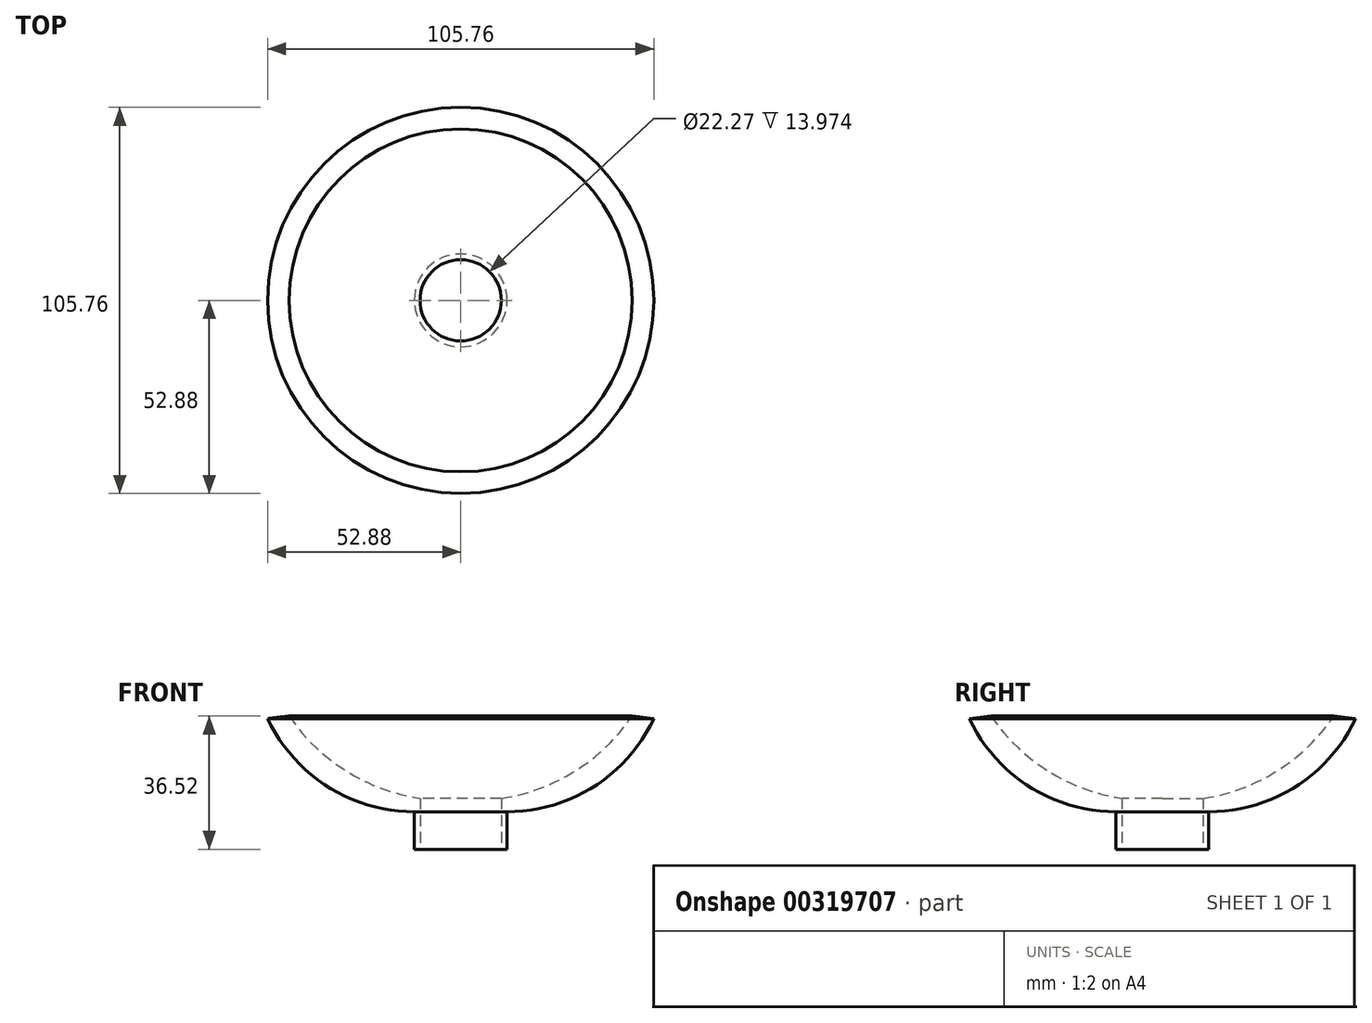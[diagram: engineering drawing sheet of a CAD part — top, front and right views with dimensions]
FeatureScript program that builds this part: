
annotation { "Feature Type Name" : "Feature", "Feature Type Description" : "" }
export const myFeature = defineFeature(function(context is Context, id is Id, definition is map)
    precondition{}
    {
        {
            var Q0;
            Q0=qCreatedBy(makeId("Front.planeOp"),FACE);
            var sketch = newSketch(context, id + "F0", { "sketchPlane" : qUnion([Q0])});
            skLineSegment(sketch, "E0", {"start": v(0, 0) * mm, "end": v(-12.7, 0) * mm});
            skLineSegment(sketch, "E1", {"start": v(-12.7, 0) * mm, "end": v(-12.7, 10.28) * mm});
            skLineSegment(sketch, "E2", {"start": v(0, 0) * mm, "end": v(0, 10.28) * mm});
            skArc(sketch, "E3", {"start": v(0, 10.28) * mm, "mid": v(23.79, 17.23) * mm, "end": v(40.18, 35.8) * mm});
            skLineSegment(sketch, "E4", {"start": v(-12.7, 10.28) * mm, "end": v(-12.7, 13.47) * mm});
            skArc(sketch, "E5", {"start": v(-12.7, 13.47) * mm, "mid": v(13.83, 18.8) * mm, "end": v(34.27, 36.52) * mm});
            skPoint(sketch, "E6.orphan", {"position": v(-12.7, 16.66) * mm});
            skLineSegment(sketch, "E7", {"start": v(34.27, 36.52) * mm, "end": v(40.18, 35.8) * mm});
            skSolve(sketch);
        }
        {
            var Q0;
            Q0 = qSketchRegion(id + "F0", true);
            var Q1;
            Q1=sQuery(id+"F0.wireOp",EDGE,"E1");
            revolve(context, id + "F1", {"entities" : qUnion([Q0]), "axis" : qUnion([Q1]), "revolveType" : RevolveType.FULL});
        }
        {
            var Q0;
            Q0=makeQuery(id+"F1.opRevolve","SWEPT_FACE",FACE,{"disambiguationData":[OSD([sQuery(id+"F0.wireOp",EDGE,"E0")])]});
            var sketch = newSketch(context, id + "F2", { "sketchPlane" : qUnion([Q0])});
            skCircle(sketch, "E8", {"center": v(-12.7, 0) * mm, "radius": 11.13 * mm});
            skSolve(sketch);
        }
        {
            var Q0;
            Q0 = qSketchRegion(id + "F2", true);
            extrude(context, id + "F3", {"entities" : qUnion([Q0]), "operationType" : NewBodyOperationType.REMOVE, "oppositeDirection" : true, "depth" : 25.4 * mm});
        }
    });
